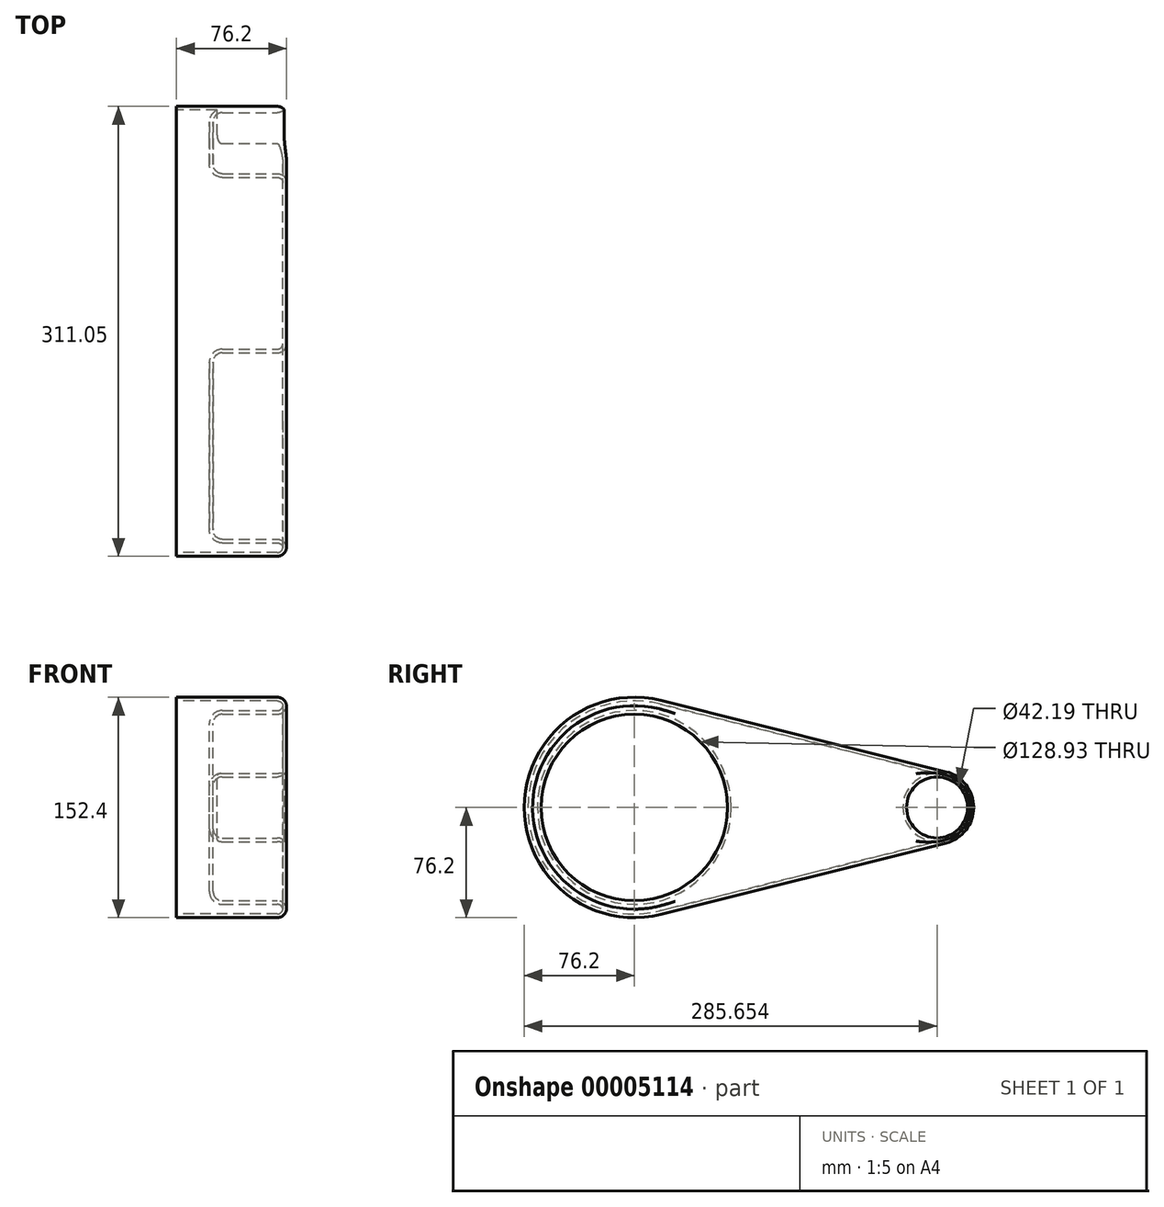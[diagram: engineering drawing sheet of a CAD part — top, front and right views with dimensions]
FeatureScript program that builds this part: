
annotation { "Feature Type Name" : "Feature", "Feature Type Description" : "" }
export const myFeature = defineFeature(function(context is Context, id is Id, definition is map)
    precondition{}
    {
        {
            var Q0;
            Q0=qCreatedBy(makeId("Right.planeOp"),FACE);
            var sketch = newSketch(context, id + "F0", { "sketchPlane" : qUnion([Q0])});
            skCircle(sketch, "E0", {"center": v(0, 0) * mm, "radius": 76.2 * mm});
            skCircle(sketch, "E1", {"center": v(209.45, 0) * mm, "radius": 25.4 * mm});
            skLineSegment(sketch, "E2", {"start": v(18.48, 73.92) * mm, "end": v(215.61, 24.64) * mm});
            skLineSegment(sketch, "E3", {"start": v(18.48, -73.92) * mm, "end": v(215.61, -24.64) * mm});
            skSolve(sketch);
        }
        {
            var Q0;
            {var subQ1=sQuery(id+"F0.wireOp",EDGE,"E2");Q0=makeQuery(id+"F0.imprint","IMPRINT",FACE,{"disambiguationData":[TD([[makeQuery(id+"F0.imprint","IMPRINT",EDGE,{"derivedFrom":subQ1}),-1.0]])]});}
            var Q1;
            {var subQ0=sQuery(id+"F0.wireOp",EDGE,"E0");var subQ2=makeQuery(id+"F0.imprint","INTERSECT",VERTEX,{"derivedFrom":[subQ0,sQuery(id+"F0.wireOp",EDGE,"E2")]});Q1=makeQuery(id+"F0.imprint","IMPRINT",FACE,{"disambiguationData":[TD([[makeQuery(id+"F0.imprint","IMPRINT",EDGE,{"disambiguationData":[TD([[subQ2,-1.0]])],"derivedFrom":subQ0}),1.0]])]});}
            var Q2;
            {var subQ0=sQuery(id+"F0.wireOp",EDGE,"E1");var subQ2=makeQuery(id+"F0.imprint","INTERSECT",VERTEX,{"derivedFrom":[subQ0,sQuery(id+"F0.wireOp",EDGE,"E2")]});Q2=makeQuery(id+"F0.imprint","IMPRINT",FACE,{"disambiguationData":[TD([[makeQuery(id+"F0.imprint","IMPRINT",EDGE,{"disambiguationData":[TD([[subQ2,-1.0]])],"derivedFrom":subQ0}),1.0]])]});}
            extrude(context, id + "F1", {"entities" : qUnion([Q0, Q1, Q2]), "depth" : 76.2 * mm});
        }
        {
            var Q0;
            Q0=makeQuery(id+"F1.opExtrude","CAP_FACE",FACE,{"disambiguationData":[OSD([sQuery(id+"F0.wireOp",EDGE,"E0"),sQuery(id+"F0.wireOp",EDGE,"E1"),sQuery(id+"F0.wireOp",EDGE,"E2"),sQuery(id+"F0.wireOp",EDGE,"E3")])],"isStart":false});
            var sketch = newSketch(context, id + "F2", { "sketchPlane" : qUnion([Q0])});
            skCircle(sketch, "E4", {"center": v(0, 0) * mm, "radius": 64.47 * mm});
            skCircle(sketch, "E5", {"center": v(209.45, 0) * mm, "radius": 21.1 * mm});
            skSolve(sketch);
        }
        {
            var Q0;
            Q0=makeQuery(id+"F2.imprint","IMPRINT",FACE,{"disambiguationData":[TD([[makeQuery(id+"F2.imprint","IMPRINT",EDGE,{"derivedFrom":sQuery(id+"F2.wireOp",EDGE,"E4")}),1.0]])]});
            var Q1;
            Q1=makeQuery(id+"F2.imprint","IMPRINT",FACE,{"disambiguationData":[TD([[makeQuery(id+"F2.imprint","IMPRINT",EDGE,{"derivedFrom":sQuery(id+"F2.wireOp",EDGE,"E5")}),1.0]])]});
            extrude(context, id + "F3", {"entities" : qUnion([Q0, Q1]), "operationType" : NewBodyOperationType.REMOVE, "oppositeDirection" : true, "depth" : 50.8 * mm});
        }
        {
            var Q0;
            Q0=makeQuery(id+"F1.opExtrude","CAP_FACE",FACE,{"disambiguationData":[OSD([sQuery(id+"F0.wireOp",EDGE,"E0"),sQuery(id+"F0.wireOp",EDGE,"E1"),sQuery(id+"F0.wireOp",EDGE,"E2"),sQuery(id+"F0.wireOp",EDGE,"E3")])],"isStart":false});
            var Q1;
            Q1=makeQuery(id+"F3.boolean.opBoolean","COPY",EDGE,{"derivedFrom":makeQuery(id+"F3.opExtrude","CAP_EDGE",EDGE,{"disambiguationData":[OSD([sQuery(id+"F2.wireOp",EDGE,"E4")])],"isStart":false})});
            var Q2;
            Q2=makeQuery(id+"F3.boolean.opBoolean","COPY",EDGE,{"derivedFrom":makeQuery(id+"F3.opExtrude","CAP_EDGE",EDGE,{"disambiguationData":[OSD([sQuery(id+"F2.wireOp",EDGE,"E5")])],"isStart":false})});
            fillet(context, id + "F4", {"entities" : qUnion([Q0, Q1, Q2]), "radius" : 6.35 * mm, "tangentPropagation" : true, "allowEdgeOverflow" : false});
        }
        {
            var Q0;
            Q0=makeQuery(id+"F1.opExtrude","CAP_FACE",FACE,{"disambiguationData":[OSD([sQuery(id+"F0.wireOp",EDGE,"E0"),sQuery(id+"F0.wireOp",EDGE,"E1"),sQuery(id+"F0.wireOp",EDGE,"E2"),sQuery(id+"F0.wireOp",EDGE,"E3")])],"isStart":true});
            shell(context, id + "F5", {"entities" : qUnion([Q0]), "thickness" : 2.54 * mm});
        }
    });
